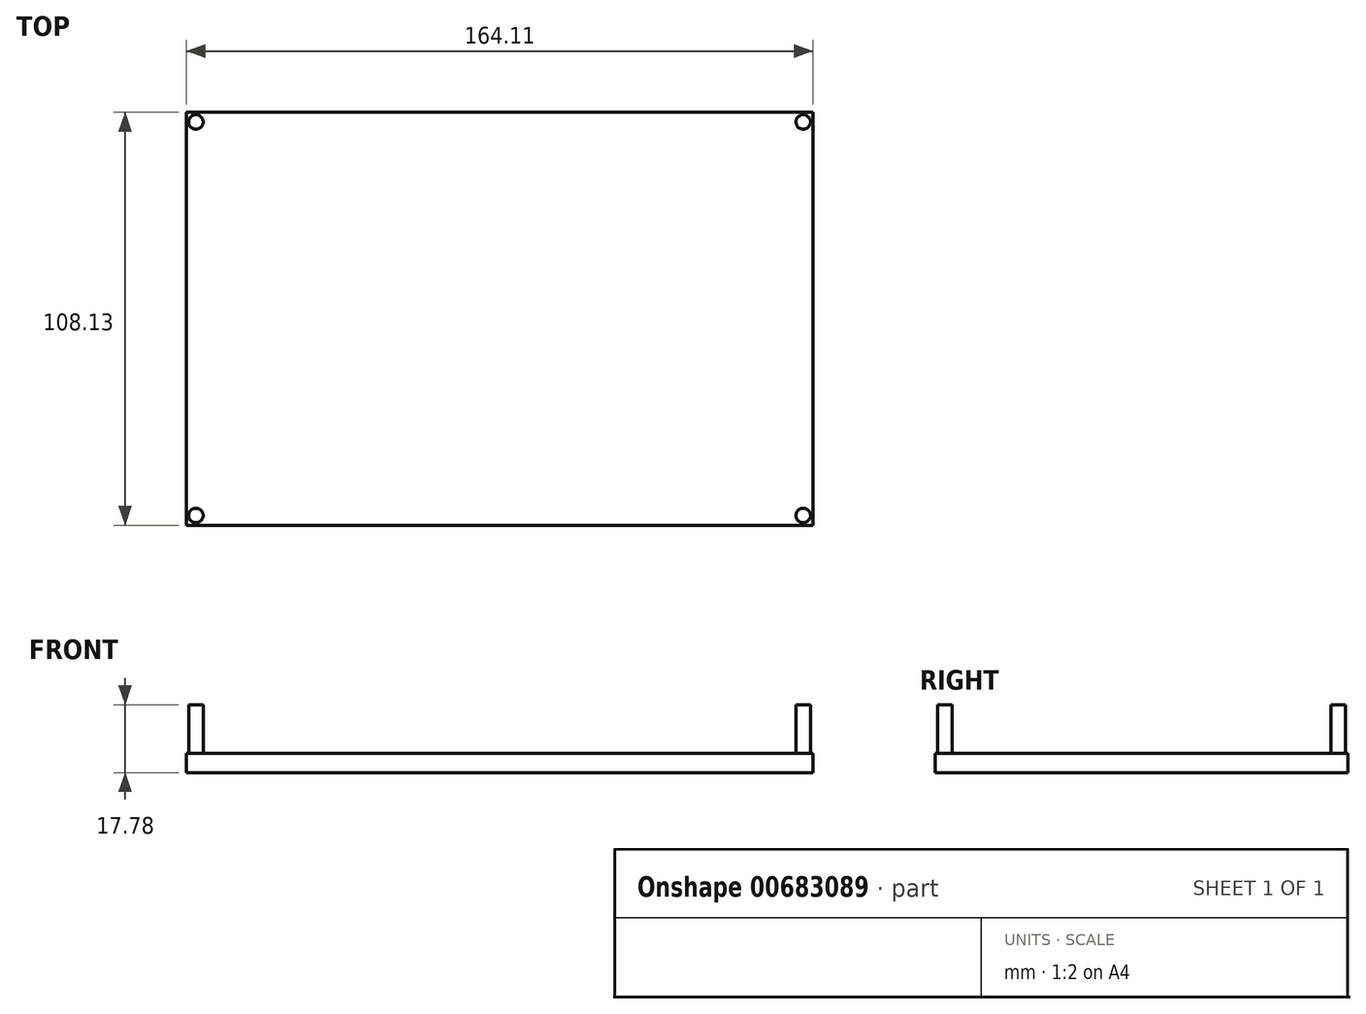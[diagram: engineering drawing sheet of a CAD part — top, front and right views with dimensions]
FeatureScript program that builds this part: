
annotation { "Feature Type Name" : "Feature", "Feature Type Description" : "" }
export const myFeature = defineFeature(function(context is Context, id is Id, definition is map)
    precondition{}
    {
        {
            var Q0;
            Q0=qCreatedBy(makeId("Top.planeOp"),FACE);
            var sketch = newSketch(context, id + "F0", { "sketchPlane" : qUnion([Q0])});
            skLineSegment(sketch, "E0.0", {"start": v(-26.64, 53.39) * mm, "end": v(-64.4, 53.39) * mm});
            skLineSegment(sketch, "E1.0", {"start": v(89.55, 53.39) * mm, "end": v(-26.64, 53.39) * mm});
            skLineSegment(sketch, "E2.0", {"start": v(-26.64, -54.74) * mm, "end": v(89.55, -54.74) * mm});
            skLineSegment(sketch, "E3.0", {"start": v(-26.64, -54.74) * mm, "end": v(-64.4, -54.74) * mm});
            skLineSegment(sketch, "E4.0", {"start": v(-69.48, 48.3) * mm, "end": v(-69.48, -49.66) * mm});
            skLineSegment(sketch, "E5", {"start": v(-69.48, 48.3) * mm, "end": v(-69.48, 53.39) * mm});
            skLineSegment(sketch, "E6", {"start": v(-69.48, 53.39) * mm, "end": v(-64.4, 53.39) * mm});
            skLineSegment(sketch, "E7", {"start": v(89.55, 53.39) * mm, "end": v(94.63, 53.39) * mm});
            skLineSegment(sketch, "E8", {"start": v(94.63, 53.39) * mm, "end": v(94.63, 12.15) * mm});
            skLineSegment(sketch, "E9", {"start": v(-69.48, -49.66) * mm, "end": v(-69.48, -54.74) * mm});
            skLineSegment(sketch, "E10", {"start": v(-69.48, -54.74) * mm, "end": v(-64.4, -54.74) * mm});
            skLineSegment(sketch, "E11", {"start": v(89.55, -54.74) * mm, "end": v(94.63, -54.74) * mm});
            skLineSegment(sketch, "E12", {"start": v(94.63, 12.15) * mm, "end": v(94.63, -54.74) * mm});
            skSolve(sketch);
        }
        {
            var Q0;
            Q0=qCreatedBy(makeId("Top.planeOp"),FACE);
            var sketch = newSketch(context, id + "F1", { "sketchPlane" : qUnion([Q0])});
            skLineSegment(sketch, "E13", {"start": v(-26.64, -49.66) * mm, "end": v(-64.4, -49.66) * mm});
            skLineSegment(sketch, "E14", {"start": v(-26.64, 48.3) * mm, "end": v(-64.4, 48.3) * mm});
            skLineSegment(sketch, "E15", {"start": v(-26.64, -49.66) * mm, "end": v(89.55, -49.66) * mm});
            skLineSegment(sketch, "E16", {"start": v(89.55, -49.66) * mm, "end": v(89.55, 48.3) * mm});
            skLineSegment(sketch, "E17", {"start": v(89.55, 48.3) * mm, "end": v(-26.64, 48.3) * mm});
            skLineSegment(sketch, "E18", {"start": v(-64.4, 48.3) * mm, "end": v(-64.4, -49.66) * mm});
            skLineSegment(sketch, "E19.0", {"start": v(-26.64, 53.39) * mm, "end": v(-64.4, 53.39) * mm});
            skLineSegment(sketch, "E20.0", {"start": v(89.55, 53.39) * mm, "end": v(-26.64, 53.39) * mm});
            skLineSegment(sketch, "E21.0", {"start": v(-26.64, -54.74) * mm, "end": v(89.55, -54.74) * mm});
            skLineSegment(sketch, "E22.0", {"start": v(-26.64, -54.74) * mm, "end": v(-64.4, -54.74) * mm});
            skLineSegment(sketch, "E23.0", {"start": v(-69.48, 48.3) * mm, "end": v(-69.48, -49.66) * mm});
            skLineSegment(sketch, "E24", {"start": v(-69.48, 48.3) * mm, "end": v(-69.48, 53.39) * mm});
            skLineSegment(sketch, "E25", {"start": v(-69.48, 53.39) * mm, "end": v(-64.4, 53.39) * mm});
            skLineSegment(sketch, "E26", {"start": v(89.55, 53.39) * mm, "end": v(94.63, 53.39) * mm});
            skLineSegment(sketch, "E27", {"start": v(94.63, 53.39) * mm, "end": v(94.63, 12.15) * mm});
            skLineSegment(sketch, "E28", {"start": v(-69.48, -49.66) * mm, "end": v(-69.48, -54.74) * mm});
            skLineSegment(sketch, "E29", {"start": v(-69.48, -54.74) * mm, "end": v(-64.4, -54.74) * mm});
            skLineSegment(sketch, "E30", {"start": v(89.55, -54.74) * mm, "end": v(94.63, -54.74) * mm});
            skLineSegment(sketch, "E31", {"start": v(94.63, 12.15) * mm, "end": v(94.63, -54.74) * mm});
            skCircle(sketch, "E32", {"center": v(-66.94, -52.2) * mm, "radius": 1.9 * mm});
            skCircle(sketch, "E33", {"center": v(92.1, -52.2) * mm, "radius": 1.9 * mm});
            skCircle(sketch, "E34", {"center": v(92.1, 50.85) * mm, "radius": 1.9 * mm});
            skCircle(sketch, "E35", {"center": v(-66.94, 50.85) * mm, "radius": 1.9 * mm});
            skSolve(sketch);
        }
        {
            var Q0;
            Q0=makeQuery(id+"F0.imprint","IMPRINT",FACE,{"disambiguationData":[TD([[makeQuery(id+"F0.imprint","IMPRINT",EDGE,{"derivedFrom":sQuery(id+"F0.wireOp",EDGE,"E0.0")}),1.0]])]});
            extrude(context, id + "F2", {"entities" : qUnion([Q0]), "oppositeDirection" : true, "depth" : 5.08 * mm, "offsetDistance" : 25.4 * mm});
        }
        {
            var Q0;
            Q0=makeQuery(id+"F1.imprint","IMPRINT",FACE,{"disambiguationData":[TD([[makeQuery(id+"F1.imprint","IMPRINT",EDGE,{"derivedFrom":sQuery(id+"F1.wireOp",EDGE,"E32")}),1.0]])]});
            var Q1;
            Q1=makeQuery(id+"F1.imprint","IMPRINT",FACE,{"disambiguationData":[TD([[makeQuery(id+"F1.imprint","IMPRINT",EDGE,{"derivedFrom":sQuery(id+"F1.wireOp",EDGE,"E35")}),1.0]])]});
            var Q2;
            Q2=makeQuery(id+"F1.imprint","IMPRINT",FACE,{"disambiguationData":[TD([[makeQuery(id+"F1.imprint","IMPRINT",EDGE,{"derivedFrom":sQuery(id+"F1.wireOp",EDGE,"E34")}),1.0]])]});
            var Q3;
            Q3=makeQuery(id+"F1.imprint","IMPRINT",FACE,{"disambiguationData":[TD([[makeQuery(id+"F1.imprint","IMPRINT",EDGE,{"derivedFrom":sQuery(id+"F1.wireOp",EDGE,"E33")}),1.0]])]});
            extrude(context, id + "F3", {"entities" : qUnion([Q0, Q1, Q2, Q3]), "operationType" : NewBodyOperationType.ADD, "depth" : 12.7 * mm, "offsetDistance" : 25.4 * mm});
        }
    });
